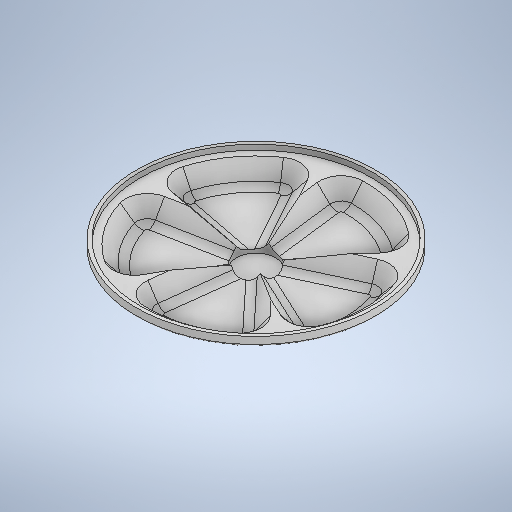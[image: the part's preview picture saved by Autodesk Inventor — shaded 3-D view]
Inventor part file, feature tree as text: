
AUTODESK INVENTOR PART (.ipt)
format: ipt  version: 2025.3 (Build 293356000, 356)  size: 733,184 bytes
history: native  units: mm
features: sketch x4, extrude x3, fillet x3, shell x1
ambient origin geometry x8: Origin, YZ Plane, XZ Plane, XY Plane, X Axis, Y Axis, Z Axis, Center Point
bodies: Body1 (feature_tree)
feature tree (11):
  extrude  "Extrusión2"  Depth=1100.0mm
  fillet  "Empalme2"  Radius=50.0mm
  extrude  "Extrusión3"  Depth=8.726646mm
  fillet  "Empalme3"  Radius=50.0mm
  extrude  "Extrusión4"  Depth=80.0mm
  fillet  "Empalme4"  Radius=1370.0mm
  shell  "Vaciado2"  Thickness=50.0mm
  sketch  "Boceto5"  dims[d21=50.0mm d22=8.726646mm d23=50.0mm d25=360.0deg]
  sketch  "Boceto - Patrón circular2"  dims[d18=1370.0mm d19=1100.0mm d20=50.0mm]
  sketch  "Boceto6"  dims[d27=150.0mm d28=6.981317mm d29=80.0mm d30=1370.0mm d31=50.0mm d32=0.0mm]
  sketch  "Boceto7"  dims[d33=10.0mm d34=265.0mm d35=170.0mm d36=0.0mm d37=10.0mm d38=20.0mm]
